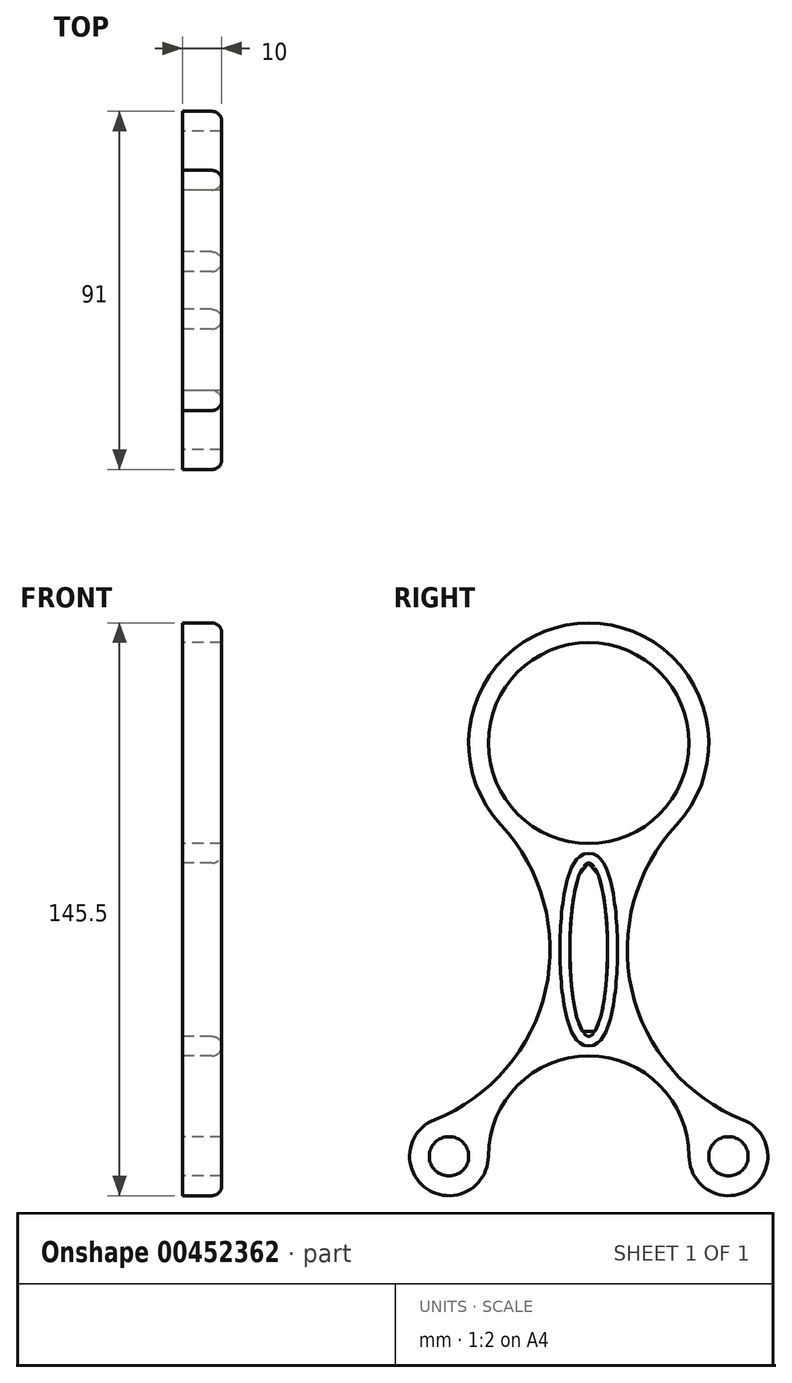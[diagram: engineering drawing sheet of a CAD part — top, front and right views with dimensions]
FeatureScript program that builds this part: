
annotation { "Feature Type Name" : "Feature", "Feature Type Description" : "" }
export const myFeature = defineFeature(function(context is Context, id is Id, definition is map)
    precondition{}
    {
        {
            var Q0;
            Q0=qCreatedBy(makeId("Right.planeOp"),FACE);
            var sketch = newSketch(context, id + "F0", { "sketchPlane" : qUnion([Q0])});
            skArc(sketch, "E0", {"start": v(25.5, 10) * mm, "mid": v(0, 35.5) * mm, "end": v(-25.5, 10) * mm});
            skArc(sketch, "E1", {"start": v(25.5, 10) * mm, "mid": v(41.12, 1.73) * mm, "end": v(39.18, 19.3) * mm});
            skArc(sketch, "E2", {"start": v(22.3, 94.2) * mm, "mid": v(10.95, 52.29) * mm, "end": v(39.18, 19.3) * mm});
            skArc(sketch, "E3", {"start": v(22.3, 94.2) * mm, "mid": v(0, 145.5) * mm, "end": v(-22.3, 94.2) * mm});
            skArc(sketch, "E4", {"start": v(-39.18, 19.3) * mm, "mid": v(-10.95, 52.29) * mm, "end": v(-22.3, 94.2) * mm});
            skArc(sketch, "E5", {"start": v(-39.18, 19.3) * mm, "mid": v(-41.12, 1.73) * mm, "end": v(-25.5, 10) * mm});
            skCircle(sketch, "E6", {"center": v(0, 115) * mm, "radius": 25.5 * mm});
            skLineSegment(sketch, "E7", {"start": v(-25.5, 10) * mm, "end": v(25.5, 10) * mm, "construction": true});
            skCircle(sketch, "E8", {"center": v(-35.5, 10) * mm, "radius": 5 * mm});
            skEllipse(sketch, "E9", {"center": v(0, 62.5) * mm, "majorRadius": 22 * mm, "minorRadius": 4.81 * mm, "majorAxis": v(0, 1)});
            skLineSegment(sketch, "E10", {"start": v(4.81, 62.5) * mm, "end": v(9.81, 62.5) * mm, "construction": true});
            skLineSegment(sketch, "E11", {"start": v(0, 84.5) * mm, "end": v(0, 89.5) * mm, "construction": true});
            skLineSegment(sketch, "E12", {"start": v(0, 35.5) * mm, "end": v(0, 89.5) * mm, "construction": true});
            skCircle(sketch, "E13.MirrorC", {"center": v(35.5, 10) * mm, "radius": 5 * mm});
            skArc(sketch, "E14", {"start": v(-25.5, 10) * mm, "mid": v(-29.88, 18.27) * mm, "end": v(-39.18, 19.3) * mm});
            skArc(sketch, "E15", {"start": v(39.18, 19.3) * mm, "mid": v(29.88, 18.27) * mm, "end": v(25.5, 10) * mm});
            skSolve(sketch);
        }
        {
            var Q0;
            Q0 = qSketchRegion(id + "F0", true);
            extrude(context, id + "F1", {"entities" : qUnion([Q0]), "endBound" : BoundingType.SYMMETRIC, "depth" : 10 * mm});
        }
        {
            var Q0;
            Q0=makeQuery(id+"F1.opExtrude","CAP_EDGE",EDGE,{"disambiguationData":[OSD([sQuery(id+"F0.wireOp",EDGE,"E5")])],"isStart":false});
            var Q1;
            Q1=makeQuery(id+"F1.opExtrude","CAP_EDGE",EDGE,{"disambiguationData":[OSD([sQuery(id+"F0.wireOp",EDGE,"E9")])],"isStart":false});
            fillet(context, id + "F2", {"entities" : qUnion([Q0, Q1]), "radius" : 2.5 * mm, "tangentPropagation" : true, "allowEdgeOverflow" : false});
        }
    });
